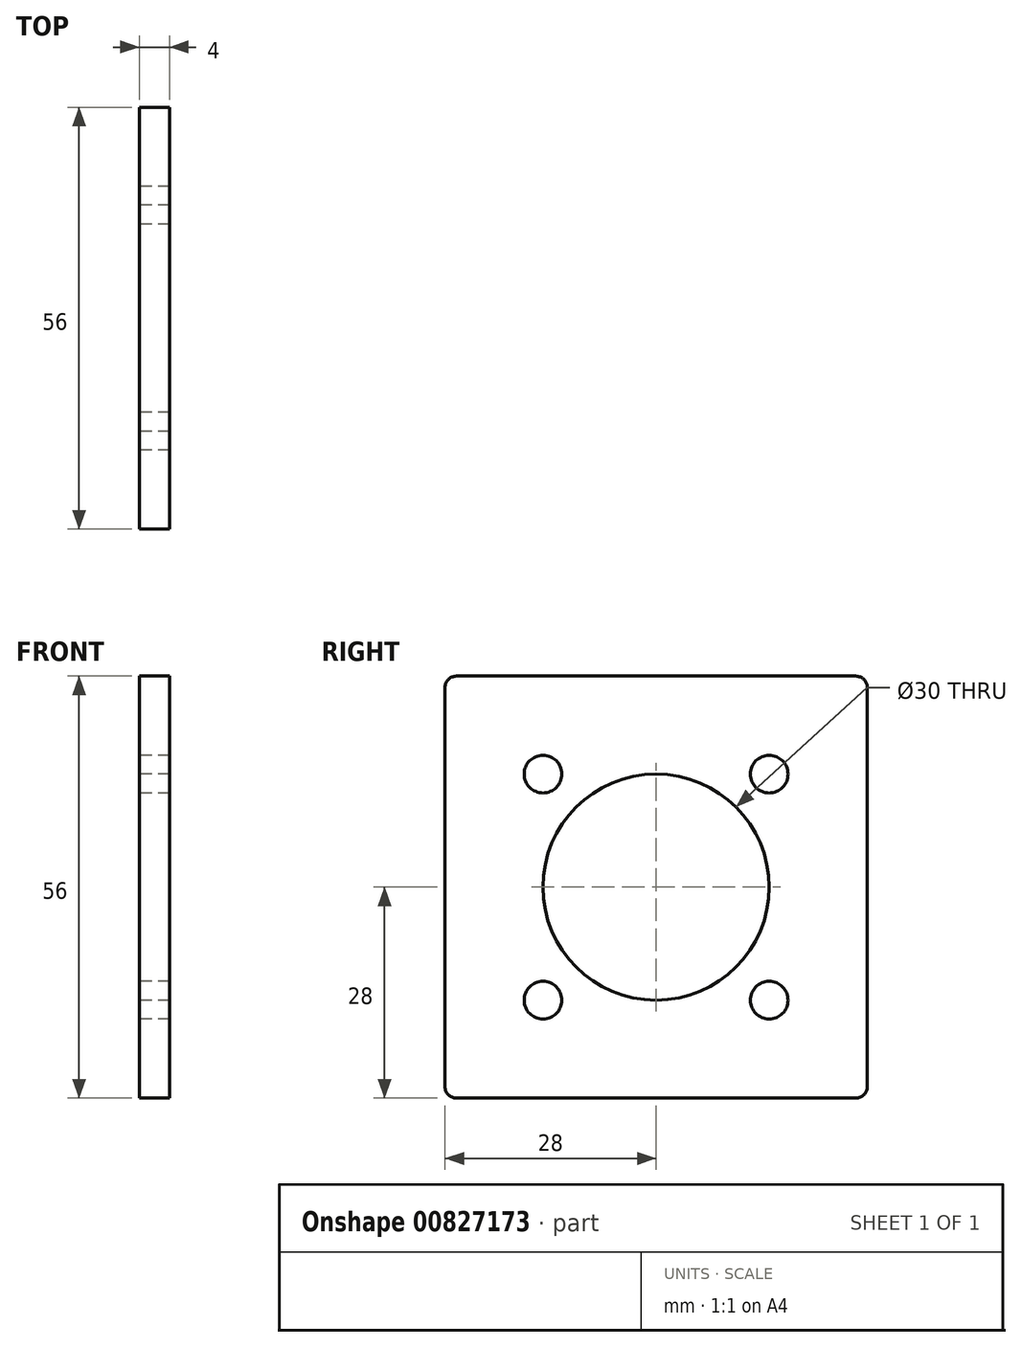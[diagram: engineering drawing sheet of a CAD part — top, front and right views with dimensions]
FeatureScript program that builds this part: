
annotation { "Feature Type Name" : "Feature", "Feature Type Description" : "" }
export const myFeature = defineFeature(function(context is Context, id is Id, definition is map)
    precondition{}
    {
        {
            var Q0;
            Q0=qCreatedBy(makeId("Right.planeOp"),FACE);
            var sketch = newSketch(context, id + "F0", { "sketchPlane" : qUnion([Q0])});
            skPoint(sketch, "E0.middle", {"position": v(0, 0) * mm});
            skLineSegment(sketch, "E1", {"start": v(0, 15) * mm, "end": v(15, 15) * mm, "construction": true});
            skLineSegment(sketch, "E2", {"start": v(15, 15) * mm, "end": v(15, -15) * mm, "construction": true});
            skLineSegment(sketch, "E3", {"start": v(15, -15) * mm, "end": v(0, -15) * mm, "construction": true});
            skLineSegment(sketch, "E4", {"start": v(0, -15) * mm, "end": v(-15, -15) * mm, "construction": true});
            skLineSegment(sketch, "E5", {"start": v(-15, -15) * mm, "end": v(-15, 15) * mm, "construction": true});
            skCircle(sketch, "E6", {"center": v(-15, 15) * mm, "radius": 2.5 * mm});
            skCircle(sketch, "E7", {"center": v(15, 15) * mm, "radius": 2.5 * mm});
            skCircle(sketch, "E8", {"center": v(-15, -15) * mm, "radius": 2.5 * mm});
            skCircle(sketch, "E9", {"center": v(15, -15) * mm, "radius": 2.5 * mm});
            skLineSegment(sketch, "E10", {"start": v(0, 28) * mm, "end": v(0, 15) * mm, "construction": true});
            skCircle(sketch, "E11", {"center": v(0, 0) * mm, "radius": 15 * mm});
            skLineSegment(sketch, "E12.bottom", {"start": v(28, 28) * mm, "end": v(-28, 28) * mm});
            skLineSegment(sketch, "E12.top", {"start": v(28, -28) * mm, "end": v(-28, -28) * mm});
            skLineSegment(sketch, "E12.left", {"start": v(28, 28) * mm, "end": v(28, -28) * mm});
            skLineSegment(sketch, "E12.right", {"start": v(-28, 28) * mm, "end": v(-28, -28) * mm});
            skLineSegment(sketch, "E13", {"start": v(-28, 0) * mm, "end": v(28, 0) * mm, "construction": true});
            skSolve(sketch);
        }
        {
            var Q0;
            Q0=makeQuery(id+"F0.imprint","IMPRINT",FACE,{"disambiguationData":[TD([[makeQuery(id+"F0.imprint","IMPRINT",EDGE,{"derivedFrom":sQuery(id+"F0.wireOp",EDGE,"E0.bottom")}),1.0]])]});
            var Q1;
            Q1=makeQuery(id+"F0.imprint","IMPRINT",FACE,{"disambiguationData":[TD([[makeQuery(id+"F0.imprint","IMPRINT",EDGE,{"derivedFrom":sQuery(id+"F0.wireOp",EDGE,"E0.left")}),-1.0]])]});
            var Q2;
            Q2=makeQuery(id+"F0.imprint","IMPRINT",FACE,{"disambiguationData":[TD([[makeQuery(id+"F0.imprint","IMPRINT",EDGE,{"derivedFrom":sQuery(id+"F0.wireOp",EDGE,"E6")}),-1.0]])]});
            extrude(context, id + "F1", {"entities" : qUnion([Q0, Q1, Q2]), "depth" : 4 * mm, "offsetDistance" : 25 * mm});
        }
        {
            var Q0;
            Q0=makeQuery(id+"F1.opExtrude","SWEPT_EDGE",EDGE,{"disambiguationData":[OSD([sQuery(id+"F0.wireOp",EDGE,"E0.bottom"),sQuery(id+"F0.wireOp",EDGE,"E0.right")])]});
            var Q1;
            Q1=makeQuery(id+"F1.opExtrude","SWEPT_EDGE",EDGE,{"disambiguationData":[OSD([sQuery(id+"F0.wireOp",EDGE,"E0.bottom"),sQuery(id+"F0.wireOp",EDGE,"E0.left")])]});
            var Q2;
            Q2=makeQuery(id+"F1.opExtrude","SWEPT_EDGE",EDGE,{"disambiguationData":[OSD([sQuery(id+"F0.wireOp",EDGE,"E0.left"),sQuery(id+"F0.wireOp",EDGE,"Z9yn4AfE-NAQi-igYc-Bxnj-cpTRAm92Y7OJ")])]});
            var Q3;
            Q3=makeQuery(id+"F1.opExtrude","SWEPT_EDGE",EDGE,{"disambiguationData":[OSD([sQuery(id+"F0.wireOp",EDGE,"E0.right"),sQuery(id+"F0.wireOp",EDGE,"Z9yn4AfE-NAQi-igYc-Bxnj-cpTRAm92Y7OJ")])]});
            var Q4;
            Q4=makeQuery(id+"F1.opExtrude","SWEPT_EDGE",EDGE,{"disambiguationData":[OSD([sQuery(id+"F0.wireOp",EDGE,"E12.bottom"),sQuery(id+"F0.wireOp",EDGE,"E12.right")])]});
            var Q5;
            Q5=makeQuery(id+"F1.opExtrude","SWEPT_EDGE",EDGE,{"disambiguationData":[OSD([sQuery(id+"F0.wireOp",EDGE,"E12.top"),sQuery(id+"F0.wireOp",EDGE,"E12.right")])]});
            var Q6;
            Q6=makeQuery(id+"F1.opExtrude","SWEPT_EDGE",EDGE,{"disambiguationData":[OSD([sQuery(id+"F0.wireOp",EDGE,"E12.top"),sQuery(id+"F0.wireOp",EDGE,"E12.left")])]});
            var Q7;
            Q7=makeQuery(id+"F1.opExtrude","SWEPT_EDGE",EDGE,{"disambiguationData":[OSD([sQuery(id+"F0.wireOp",EDGE,"E12.bottom"),sQuery(id+"F0.wireOp",EDGE,"E12.left")])]});
            fillet(context, id + "F2", {"entities" : qUnion([Q0, Q1, Q2, Q3, Q4, Q5, Q6, Q7]), "radius" : 1.5 * mm, "tangentPropagation" : true, "allowEdgeOverflow" : false});
        }
        {
            var Q0;
            Q0=makeQuery(id+"F1.opExtrude","SWEPT_BODY",BODY,{"disambiguationData":[OSD([sQuery(id+"F0.wireOp",EDGE,"E6"),sQuery(id+"F0.wireOp",EDGE,"E7"),sQuery(id+"F0.wireOp",EDGE,"E8"),sQuery(id+"F0.wireOp",EDGE,"E9"),sQuery(id+"F0.wireOp",EDGE,"E11"),sQuery(id+"F0.wireOp",EDGE,"E12.bottom"),sQuery(id+"F0.wireOp",EDGE,"E12.top"),sQuery(id+"F0.wireOp",EDGE,"E12.left"),sQuery(id+"F0.wireOp",EDGE,"E12.right")])]});
            transform(context, id + "F3", {"entities" : qUnion([Q0]), "transformType" : TransformType.TRANSLATION_3D, "dx" : 0 * mm, "dy" : 0 * mm, "dz" : 0 * mm, "makeCopy" : true});
        }
        {
            var Q0;
            Q0=makeQuery(id+"F3.opPattern","COPY",BODY,{"derivedFrom":makeQuery(id+"F1.opExtrude","SWEPT_BODY",BODY,{"disambiguationData":[OSD([sQuery(id+"F0.wireOp",EDGE,"E6"),sQuery(id+"F0.wireOp",EDGE,"E7"),sQuery(id+"F0.wireOp",EDGE,"E8"),sQuery(id+"F0.wireOp",EDGE,"E9"),sQuery(id+"F0.wireOp",EDGE,"E11"),sQuery(id+"F0.wireOp",EDGE,"E12.bottom"),sQuery(id+"F0.wireOp",EDGE,"E12.top"),sQuery(id+"F0.wireOp",EDGE,"E12.left"),sQuery(id+"F0.wireOp",EDGE,"E12.right")])]}),"instanceName":"1"});
            deleteBodies(context, id + "F4", {"entities" : qUnion([Q0])});
        }
    });
